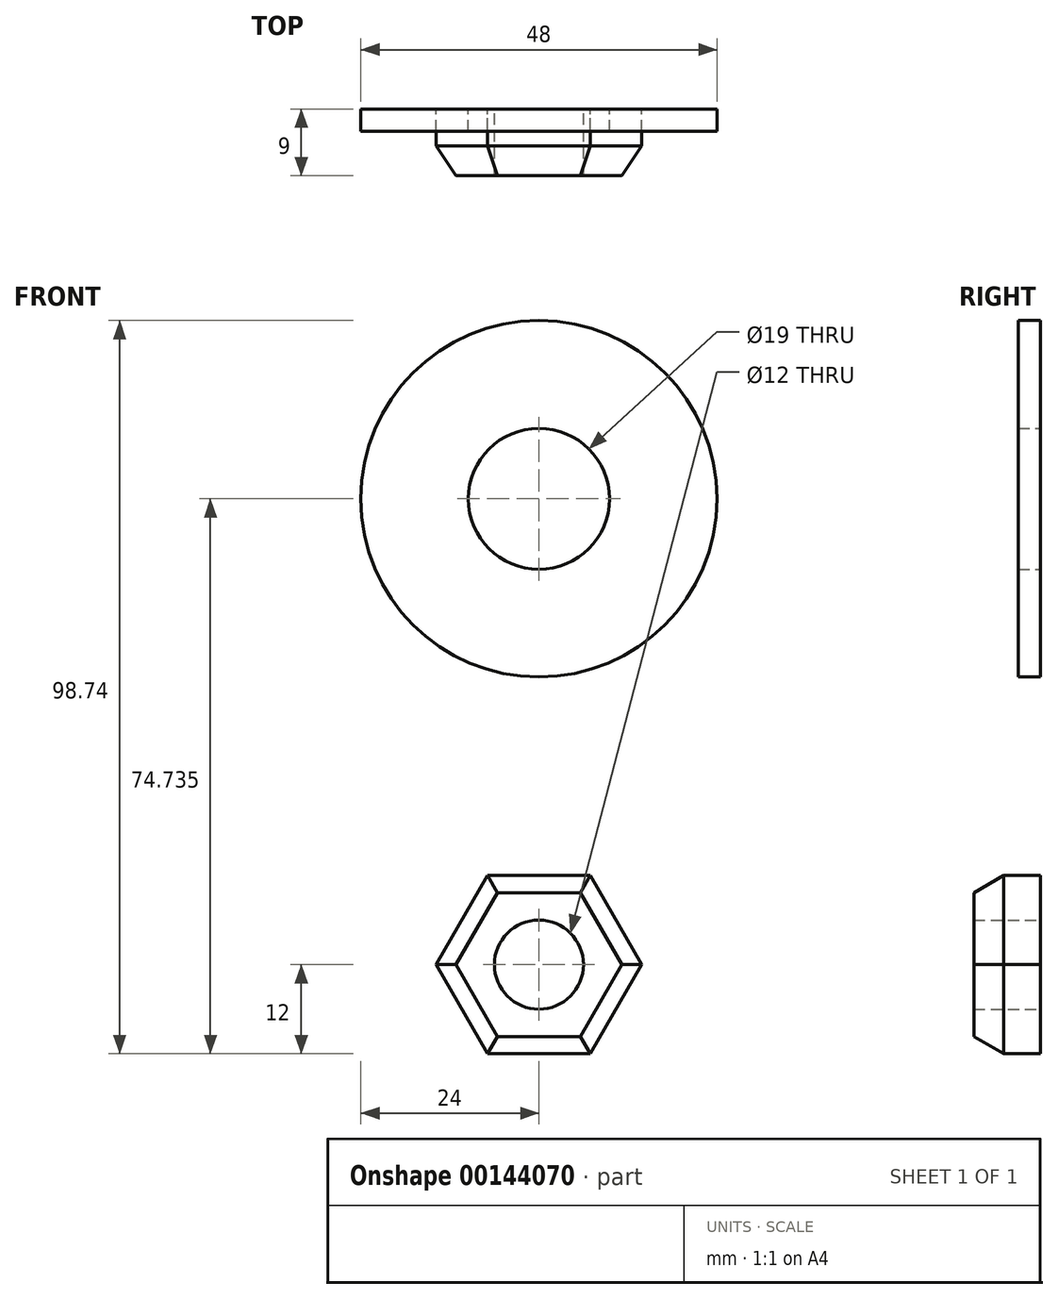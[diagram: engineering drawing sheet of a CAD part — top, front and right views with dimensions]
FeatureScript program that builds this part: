
annotation { "Feature Type Name" : "Feature", "Feature Type Description" : "" }
export const myFeature = defineFeature(function(context is Context, id is Id, definition is map)
    precondition{}
    {
        {
            var Q0;
            Q0=qCreatedBy(makeId("Front.planeOp"),FACE);
            var sketch = newSketch(context, id + "F0", { "sketchPlane" : qUnion([Q0])});
            skCircle(sketch, "E0.cCircle", {"center": v(0, 0) * mm, "radius": 12 * mm, "construction": true});
            skLineSegment(sketch, "E0.0", {"start": v(-6.93, 12) * mm, "end": v(6.93, 12) * mm});
            skLineSegment(sketch, "E0.1", {"start": v(6.93, 12) * mm, "end": v(13.86, 0) * mm});
            skLineSegment(sketch, "E0.2", {"start": v(13.86, 0) * mm, "end": v(6.93, -12) * mm});
            skLineSegment(sketch, "E0.3", {"start": v(6.93, -12) * mm, "end": v(-6.93, -12) * mm});
            skLineSegment(sketch, "E0.4", {"start": v(-6.93, -12) * mm, "end": v(-13.86, 0) * mm});
            skLineSegment(sketch, "E0.5", {"start": v(-13.86, 0) * mm, "end": v(-6.93, 12) * mm});
            skPoint(sketch, "E0.0.midPoint", {"position": v(0, 12) * mm});
            skCircle(sketch, "E1", {"center": v(0, 0) * mm, "radius": 6 * mm});
            skSolve(sketch);
        }
        {
            var Q0;
            Q0 = qSketchRegion(id + "F0", true);
            extrude(context, id + "F1", {"entities" : qUnion([Q0]), "depth" : 9 * mm});
        }
        {
            var Q0;
            Q0=qCreatedBy(makeId("Front.planeOp"),FACE);
            var sketch = newSketch(context, id + "F2", { "sketchPlane" : qUnion([Q0])});
            skCircle(sketch, "E2", {"center": v(0, 62.74) * mm, "radius": 24 * mm});
            skCircle(sketch, "E3", {"center": v(0, 62.74) * mm, "radius": 9.5 * mm});
            skSolve(sketch);
        }
        {
            var Q0;
            Q0=makeQuery(id+"F2.imprint","IMPRINT",FACE,{"disambiguationData":[TD([[makeQuery(id+"F2.imprint","IMPRINT",EDGE,{"derivedFrom":sQuery(id+"F2.wireOp",EDGE,"E2")}),1.0]])]});
            extrude(context, id + "F3", {"entities" : qUnion([Q0]), "depth" : 3 * mm});
        }
        {
            var Q0;
            Q0=makeQuery(id+"F1.opExtrude","CAP_EDGE",EDGE,{"disambiguationData":[OSD([sQuery(id+"F0.wireOp",EDGE,"E0.4")])],"isStart":false});
            var Q1;
            Q1=makeQuery(id+"F1.opExtrude","CAP_EDGE",EDGE,{"disambiguationData":[OSD([sQuery(id+"F0.wireOp",EDGE,"E0.3")])],"isStart":false});
            var Q2;
            Q2=makeQuery(id+"F1.opExtrude","CAP_EDGE",EDGE,{"disambiguationData":[OSD([sQuery(id+"F0.wireOp",EDGE,"E0.2")])],"isStart":false});
            var Q3;
            Q3=makeQuery(id+"F1.opExtrude","CAP_EDGE",EDGE,{"disambiguationData":[OSD([sQuery(id+"F0.wireOp",EDGE,"E0.1")])],"isStart":false});
            var Q4;
            Q4=makeQuery(id+"F1.opExtrude","CAP_EDGE",EDGE,{"disambiguationData":[OSD([sQuery(id+"F0.wireOp",EDGE,"E0.0")])],"isStart":false});
            var Q5;
            Q5=makeQuery(id+"F1.opExtrude","CAP_EDGE",EDGE,{"disambiguationData":[OSD([sQuery(id+"F0.wireOp",EDGE,"E0.5")])],"isStart":false});
            chamfer(context, id + "F4", {"entities" : qUnion([Q0, Q1, Q2, Q3, Q4, Q5]), "chamferType" : ChamferType.OFFSET_ANGLE, "width" : 4 * mm, "oppositeDirection" : false, "angle" : 30 * degree, "tangentPropagation" : true});
        }
    });
